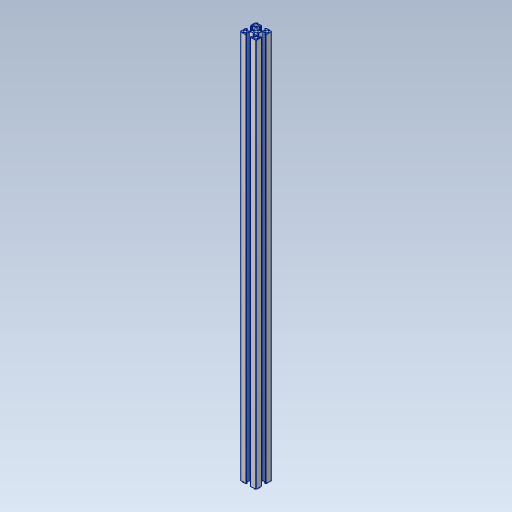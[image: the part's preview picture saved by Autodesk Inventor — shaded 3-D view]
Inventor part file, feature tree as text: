
AUTODESK INVENTOR PART (.ipt)
format: ipt  version: 2021 (Build 250183000, 183)  size: 214,528 bytes
history: native  units: mm
features: other x3, extrude x1
ambient origin geometry x8: Origin, YZ Plane, XZ Plane, XY Plane, X Axis, Y Axis, Z Axis, Center Point
bodies: Body1 (feature_tree)
feature tree (4):
  other  "솔리드1"
  other  "df_2020.dwg"
  extrude  "500mm 2020"  Depth=500.0mm TaperAngle=0.0deg
  other  "2020_Base"
